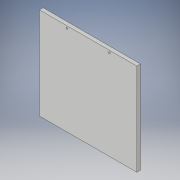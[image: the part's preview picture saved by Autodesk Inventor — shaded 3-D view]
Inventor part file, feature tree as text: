
AUTODESK INVENTOR PART (.ipt)
format: ipt  version: 2019 (Build 230136000, 136)  size: 92,160 bytes
history: native  units: in
note: dims shown in document units (in); Inventor stores cm internally (conversion verified against a paired STEP export)
features: extrude x1, sketch x1
ambient origin geometry x8: Origin, YZ Plane, XZ Plane, XY Plane, X Axis, Y Axis, Z Axis, Center Point
bodies: Solid1 (feature_tree)
feature tree (2):
  extrude  "Extrusion1"  [1 undecoded]
  sketch  "Sketch1"  dims[d8=0.3937in d9=0.0in]
note: 1 required parameter value undecoded (feature->parameter linkage not recoverable at this tier; creation-order binding heuristic only, values carry confidence <= 0.55)
